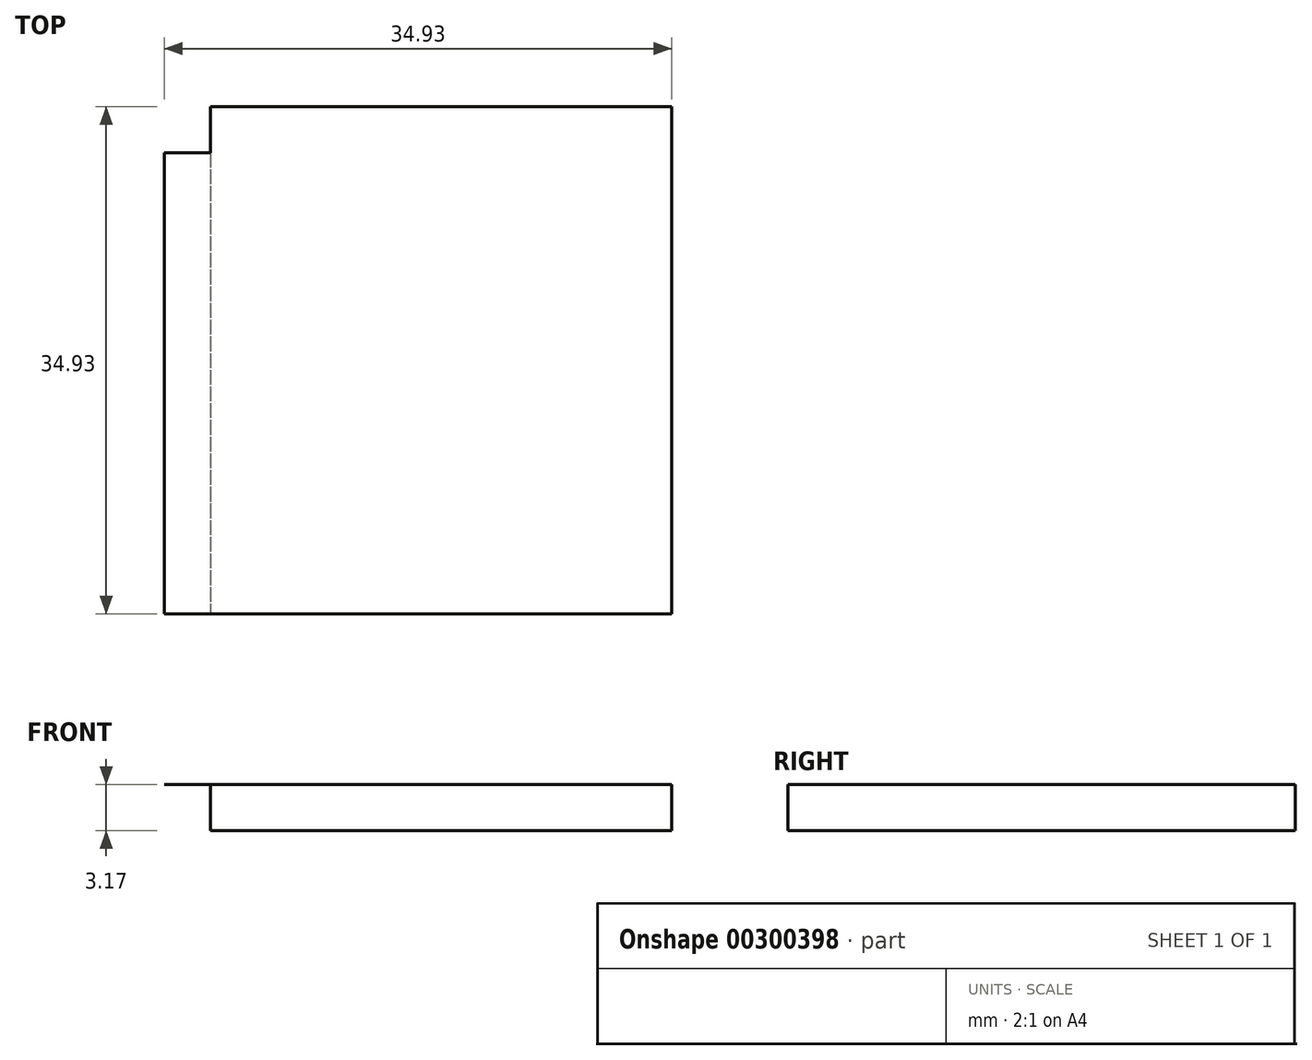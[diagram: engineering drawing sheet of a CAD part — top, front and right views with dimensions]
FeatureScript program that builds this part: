
annotation { "Feature Type Name" : "Feature", "Feature Type Description" : "" }
export const myFeature = defineFeature(function(context is Context, id is Id, definition is map)
    precondition{}
    {
        {
            var Q0;
            Q0=qCreatedBy(makeId("Top.planeOp"),FACE);
            var sketch = newSketch(context, id + "F0", { "sketchPlane" : qUnion([Q0])});
            skLineSegment(sketch, "E0.bottom", {"start": v(-15.88, 15.88) * mm, "end": v(15.88, 15.88) * mm});
            skLineSegment(sketch, "E0.top", {"start": v(-15.88, -15.88) * mm, "end": v(15.88, -15.88) * mm});
            skLineSegment(sketch, "E0.left", {"start": v(-15.88, 15.88) * mm, "end": v(-15.88, -15.88) * mm});
            skLineSegment(sketch, "E0.right", {"start": v(15.88, 15.88) * mm, "end": v(15.88, -15.88) * mm});
            skPoint(sketch, "E0.middle", {"position": v(0, 0) * mm});
            skSolve(sketch);
        }
        {
            var Q0;
            Q0 = qSketchRegion(id + "F0", true);
            extrude(context, id + "F1", {"entities" : qUnion([Q0]), "depth" : 3.17 * mm});
        }
        {
            var Q0;
            Q0=makeQuery(id+"F1.opExtrude","CAP_FACE",FACE,{"disambiguationData":[OSD([sQuery(id+"F0.wireOp",EDGE,"E0.bottom"),sQuery(id+"F0.wireOp",EDGE,"E0.top"),sQuery(id+"F0.wireOp",EDGE,"E0.left"),sQuery(id+"F0.wireOp",EDGE,"E0.right")])],"isStart":false});
            var sketch = newSketch(context, id + "F2", { "sketchPlane" : qUnion([Q0])});
            skLineSegment(sketch, "E1.bottom", {"start": v(-15.88, 15.88) * mm, "end": v(15.88, 15.88) * mm});
            skLineSegment(sketch, "E1.top", {"start": v(-15.88, 19.05) * mm, "end": v(15.88, 19.05) * mm});
            skLineSegment(sketch, "E1.left", {"start": v(-15.88, 15.88) * mm, "end": v(-15.88, 19.05) * mm});
            skLineSegment(sketch, "E1.right", {"start": v(15.88, 15.88) * mm, "end": v(15.88, 19.05) * mm});
            skSolve(sketch);
        }
        {
            var Q0;
            Q0 = qSketchRegion(id + "F2", true);
            extrude(context, id + "F3", {"entities" : qUnion([Q0]), "operationType" : NewBodyOperationType.ADD, "oppositeDirection" : true, "depth" : 3.17 * mm});
        }
        {
            var Q0;
            Q0=makeQuery(id+"F2.imprint","IMPRINT",FACE,{"disambiguationData":[TD([[makeQuery(id+"F2.imprint","IMPRINT",EDGE,{"derivedFrom":sQuery(id+"F2.wireOp",EDGE,"E1.bottom")}),-1.0]])]});
            var sketch = newSketch(context, id + "F4", { "sketchPlane" : qUnion([Q0])});
            skPoint(sketch, "E2.0", {"position": v(-15.88, 15.88) * mm});
            skPoint(sketch, "E2.1", {"position": v(-15.88, -15.88) * mm});
            skLineSegment(sketch, "E3.bottom", {"start": v(-15.88, 15.88) * mm, "end": v(-19.05, 15.88) * mm});
            skLineSegment(sketch, "E3.top", {"start": v(-15.88, -15.88) * mm, "end": v(-19.05, -15.88) * mm});
            skLineSegment(sketch, "E3.left", {"start": v(-15.88, 15.88) * mm, "end": v(-15.88, -15.88) * mm});
            skLineSegment(sketch, "E3.right", {"start": v(-19.05, 15.88) * mm, "end": v(-19.05, -15.88) * mm});
            skSolve(sketch);
        }
        {
            var Q0;
            Q0 = qSketchRegion(id + "F4", true);
            extrude(context, id + "F5", {"entities" : qUnion([Q0]), "operationType" : NewBodyOperationType.ADD, "oppositeDirection" : true, "depth" : 1 / 203.2 * mm});
        }
    });
